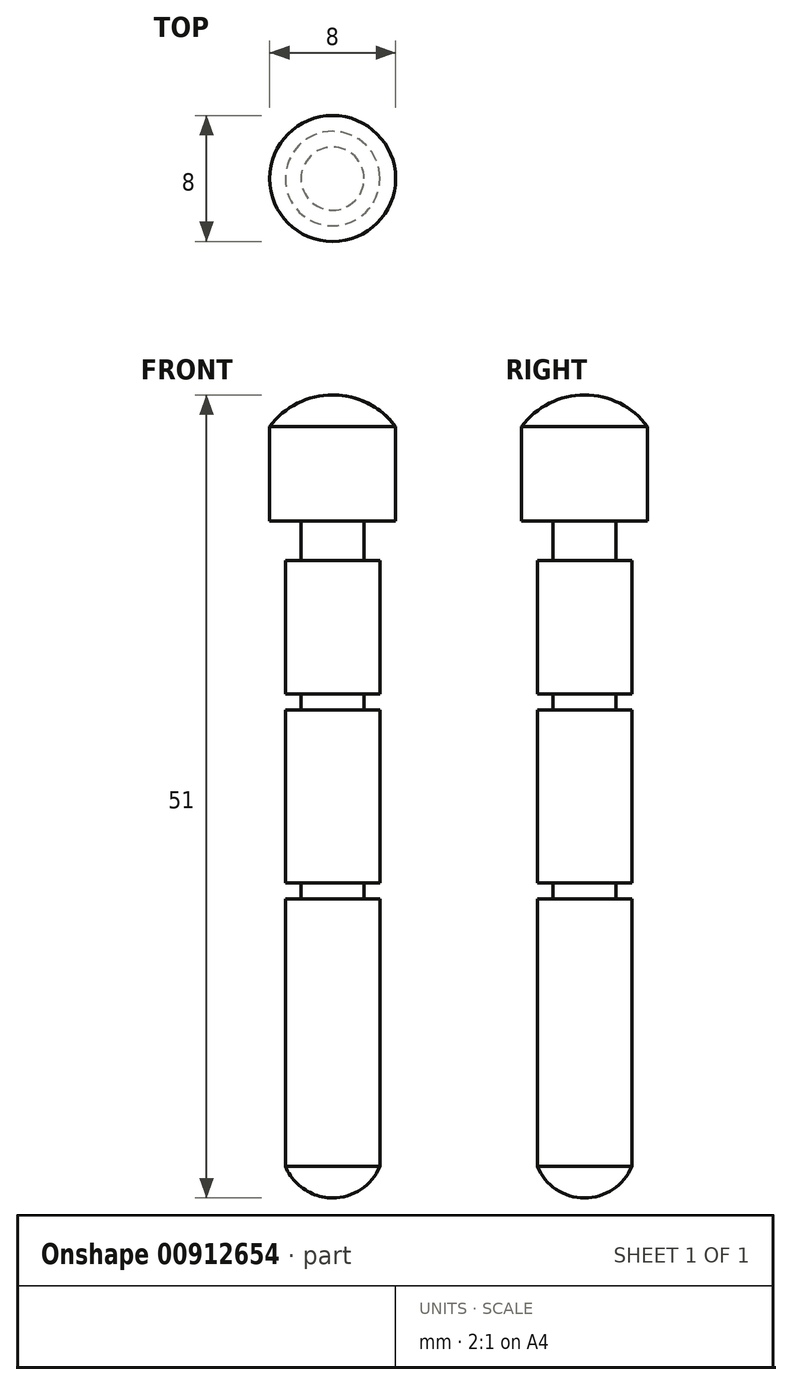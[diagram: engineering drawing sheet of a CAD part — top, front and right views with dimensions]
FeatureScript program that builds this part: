
annotation { "Feature Type Name" : "Feature", "Feature Type Description" : "" }
export const myFeature = defineFeature(function(context is Context, id is Id, definition is map)
    precondition{}
    {
        {
            var Q0;
            Q0=qCreatedBy(makeId("Front.planeOp"),FACE);
            var sketch = newSketch(context, id + "F0", { "sketchPlane" : qUnion([Q0])});
            skLineSegment(sketch, "E0", {"start": v(4, 14.88) * mm, "end": v(4, 8.88) * mm});
            skLineSegment(sketch, "E1", {"start": v(4, 8.88) * mm, "end": v(2, 8.88) * mm});
            skLineSegment(sketch, "E2", {"start": v(2, 8.88) * mm, "end": v(2, 6.38) * mm});
            skLineSegment(sketch, "E3", {"start": v(2, 6.38) * mm, "end": v(3, 6.38) * mm});
            skLineSegment(sketch, "E4", {"start": v(3, 6.38) * mm, "end": v(3, -2.12) * mm});
            skLineSegment(sketch, "E5", {"start": v(3, -2.12) * mm, "end": v(2, -2.12) * mm});
            skLineSegment(sketch, "E6", {"start": v(2, -2.12) * mm, "end": v(2, -3.12) * mm});
            skLineSegment(sketch, "E7", {"start": v(2, -3.12) * mm, "end": v(3, -3.12) * mm});
            skLineSegment(sketch, "E8", {"start": v(3, -3.12) * mm, "end": v(3, -14.12) * mm});
            skLineSegment(sketch, "E9", {"start": v(3, -14.12) * mm, "end": v(2, -14.12) * mm});
            skLineSegment(sketch, "E10", {"start": v(2, -14.12) * mm, "end": v(2, -15.12) * mm});
            skLineSegment(sketch, "E11", {"start": v(2, -15.12) * mm, "end": v(3, -15.12) * mm});
            skLineSegment(sketch, "E12", {"start": v(3, -15.12) * mm, "end": v(3, -32.12) * mm});
            skLineSegment(sketch, "E13", {"start": v(0, 16.88) * mm, "end": v(7.38, 16.88) * mm, "construction": true});
            skPoint(sketch, "E14.orphan", {"position": v(0, 7.98) * mm});
            skLineSegment(sketch, "E15", {"start": v(0, 16.88) * mm, "end": v(0, -34.12) * mm});
            skLineSegment(sketch, "E16", {"start": v(0, 11.57) * mm, "end": v(0, 13.33) * mm, "construction": true});
            skArc(sketch, "E17", {"start": v(0, -34.12) * mm, "mid": v(1.8, -33.57) * mm, "end": v(3, -32.12) * mm});
            skPoint(sketch, "E18.MirrorCS.end.orphan", {"position": v(0, -32.12) * mm});
            skPoint(sketch, "E19.orphan", {"position": v(-3, -32.12) * mm});
            skArc(sketch, "E20", {"start": v(4, 14.88) * mm, "mid": v(2.24, 16.35) * mm, "end": v(0, 16.88) * mm});
            skPoint(sketch, "E21.MirrorCS.end.orphan", {"position": v(0, 14.88) * mm});
            skPoint(sketch, "E21.MirrorCS.start.orphan", {"position": v(-4, 14.88) * mm});
            skSolve(sketch);
        }
        {
            var Q0;
            Q0=makeQuery(id+"F0.imprint","IMPRINT",FACE,{"disambiguationData":[TD([[makeQuery(id+"F0.imprint","IMPRINT",EDGE,{"derivedFrom":sQuery(id+"F0.wireOp",EDGE,"E0")}),-1.0]])]});
            var Q1;
            Q1=sQuery(id+"F0.wireOp",EDGE,"E16");
            revolve(context, id + "F1", {"surfaceOperationType" : NewSurfaceOperationType.NEW, "entities" : qUnion([Q0]), "axis" : qUnion([Q1]), "revolveType" : RevolveType.FULL});
        }
    });
